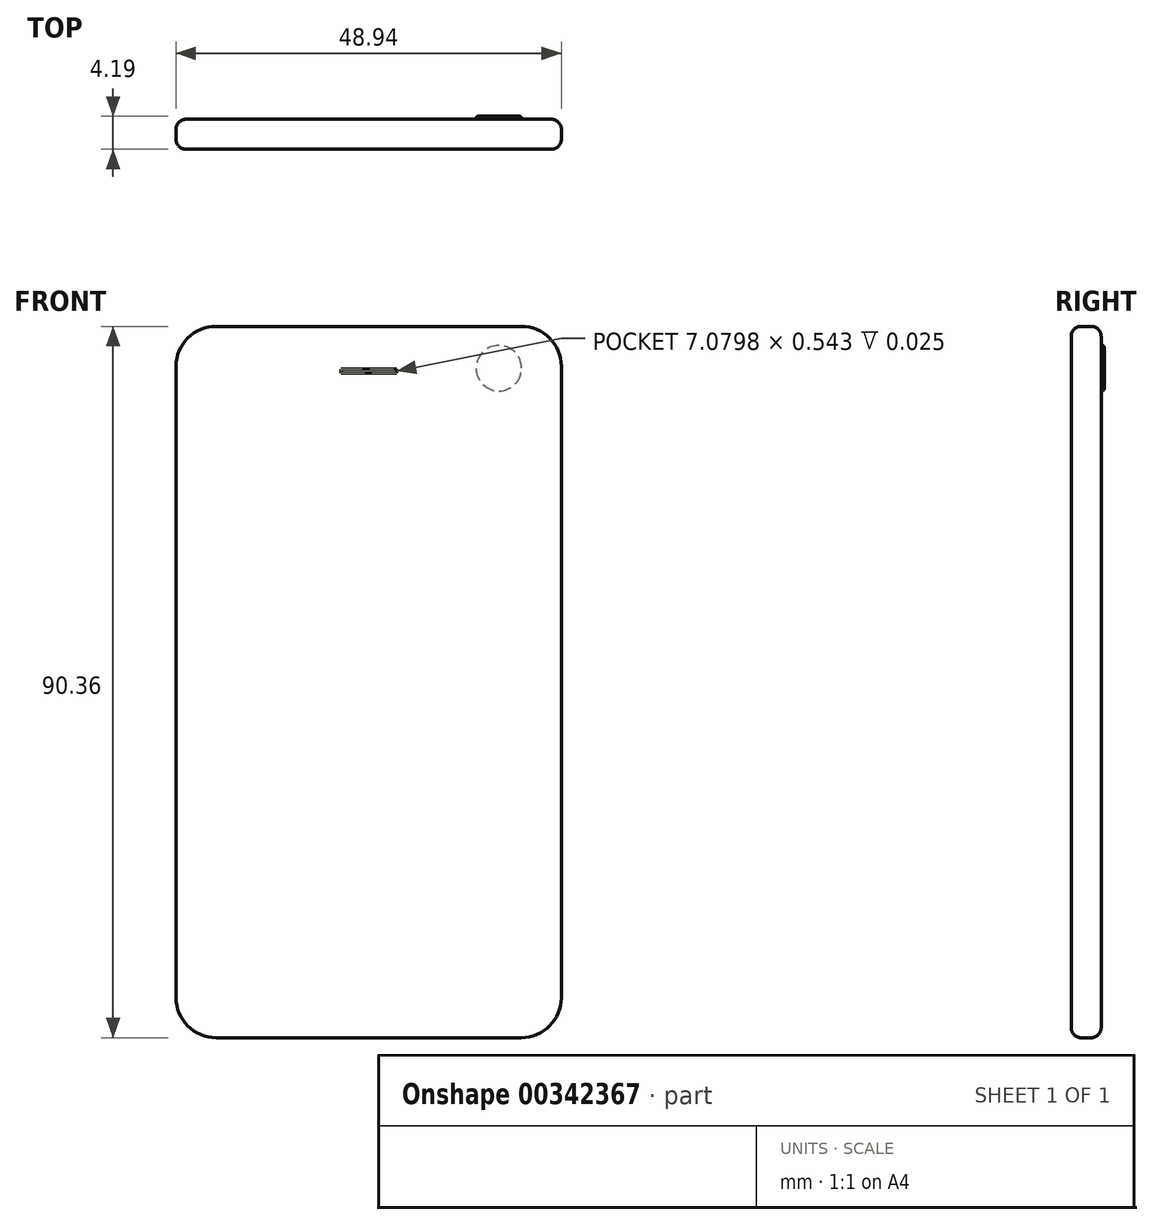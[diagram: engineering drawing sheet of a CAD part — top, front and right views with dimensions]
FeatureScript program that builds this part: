
annotation { "Feature Type Name" : "Feature", "Feature Type Description" : "" }
export const myFeature = defineFeature(function(context is Context, id is Id, definition is map)
    precondition{}
    {
        {
            var Q0;
            Q0=qCreatedBy(makeId("Front.planeOp"),FACE);
            var sketch = newSketch(context, id + "F0", { "sketchPlane" : qUnion([Q0])});
            skLineSegment(sketch, "E0.bottom", {"start": v(24.47, -45.18) * mm, "end": v(-24.47, -45.18) * mm});
            skLineSegment(sketch, "E0.top", {"start": v(24.47, 45.18) * mm, "end": v(-24.47, 45.18) * mm});
            skLineSegment(sketch, "E0.left", {"start": v(24.47, -45.18) * mm, "end": v(24.47, 45.18) * mm});
            skLineSegment(sketch, "E0.right", {"start": v(-24.47, -45.18) * mm, "end": v(-24.47, 45.18) * mm});
            skPoint(sketch, "E0.middle", {"position": v(0, 0) * mm});
            skSolve(sketch);
        }
        {
            var Q0;
            Q0=makeQuery(id+"F0.imprint","IMPRINT",FACE,{"disambiguationData":[TD([[makeQuery(id+"F0.imprint","IMPRINT",EDGE,{"derivedFrom":sQuery(id+"F0.wireOp",EDGE,"E0.bottom")}),-1.0]])]});
            extrude(context, id + "F1", {"entities" : qUnion([Q0]), "depth" : 3.8 * mm});
        }
        {
            var Q0;
            Q0=makeQuery(id+"F1.opExtrude","SWEPT_EDGE",EDGE,{"disambiguationData":[OSD([sQuery(id+"F0.wireOp",EDGE,"E0.top"),sQuery(id+"F0.wireOp",EDGE,"E0.right")])]});
            var Q1;
            Q1=makeQuery(id+"F1.opExtrude","SWEPT_EDGE",EDGE,{"disambiguationData":[OSD([sQuery(id+"F0.wireOp",EDGE,"E0.top"),sQuery(id+"F0.wireOp",EDGE,"E0.left")])]});
            var Q2;
            Q2=makeQuery(id+"F1.opExtrude","SWEPT_EDGE",EDGE,{"disambiguationData":[OSD([sQuery(id+"F0.wireOp",EDGE,"E0.bottom"),sQuery(id+"F0.wireOp",EDGE,"E0.left")])]});
            var Q3;
            Q3=makeQuery(id+"F1.opExtrude","SWEPT_EDGE",EDGE,{"disambiguationData":[OSD([sQuery(id+"F0.wireOp",EDGE,"E0.bottom"),sQuery(id+"F0.wireOp",EDGE,"E0.right")])]});
            fillet(context, id + "F2", {"entities" : qUnion([Q0, Q1, Q2, Q3]), "radius" : 5.08 * mm, "tangentPropagation" : true, "allowEdgeOverflow" : false});
        }
        {
            var Q0;
            Q0=makeQuery(id+"F1.opExtrude","CAP_EDGE",EDGE,{"disambiguationData":[OSD([sQuery(id+"F0.wireOp",EDGE,"E0.left")])],"isStart":true});
            fillet(context, id + "F3", {"entities" : qUnion([Q0]), "radius" : 1.27 * mm, "tangentPropagation" : true, "allowEdgeOverflow" : false});
        }
        {
            var Q0;
            Q0=makeQuery(id+"F1.opExtrude","CAP_EDGE",EDGE,{"disambiguationData":[OSD([sQuery(id+"F0.wireOp",EDGE,"E0.top")])],"isStart":false});
            fillet(context, id + "F4", {"entities" : qUnion([Q0]), "radius" : 1.27 * mm, "tangentPropagation" : true, "allowEdgeOverflow" : false});
        }
        {
            var Q0;
            Q0=makeQuery(id+"F1.opExtrude","CAP_FACE",FACE,{"disambiguationData":[OSD([sQuery(id+"F0.wireOp",EDGE,"E0.bottom"),sQuery(id+"F0.wireOp",EDGE,"E0.top"),sQuery(id+"F0.wireOp",EDGE,"E0.left"),sQuery(id+"F0.wireOp",EDGE,"E0.right")])],"isStart":false});
            var sketch = newSketch(context, id + "F5", { "sketchPlane" : qUnion([Q0])});
            skLineSegment(sketch, "E1.bottom", {"start": v(21.18, -35.06) * mm, "end": v(-21.18, -35.06) * mm});
            skLineSegment(sketch, "E1.top", {"start": v(21.18, 35.06) * mm, "end": v(-21.18, 35.06) * mm});
            skLineSegment(sketch, "E1.left", {"start": v(21.18, -35.06) * mm, "end": v(21.18, 35.06) * mm});
            skLineSegment(sketch, "E1.right", {"start": v(-21.18, -35.06) * mm, "end": v(-21.18, 35.06) * mm});
            skPoint(sketch, "E1.middle", {"position": v(0, 0) * mm});
            skSolve(sketch);
        }
        {
            var Q0;
            Q0=makeQuery(id+"F5.imprint","IMPRINT",FACE,{"disambiguationData":[TD([[makeQuery(id+"F5.imprint","IMPRINT",EDGE,{"derivedFrom":sQuery(id+"F5.wireOp",EDGE,"E1.bottom")}),1.0]])]});
            var sketch = newSketch(context, id + "F6", { "sketchPlane" : qUnion([Q0])});
            skCircle(sketch, "E2", {"center": v(0, -39.3) * mm, "radius": 3.86 * mm});
            skCircle(sketch, "E3", {"center": v(0, -39.3) * mm, "radius": 3.2 * mm});
            skSolve(sketch);
        }
        {
            var Q0;
            Q0=makeQuery(id+"F5.imprint","IMPRINT",FACE,{"disambiguationData":[TD([[makeQuery(id+"F5.imprint","IMPRINT",EDGE,{"derivedFrom":sQuery(id+"F5.wireOp",EDGE,"E1.bottom")}),1.0]])]});
            var sketch = newSketch(context, id + "F7", { "sketchPlane" : qUnion([Q0])});
            skLineSegment(sketch, "E4.bottom", {"start": v(3.54, 39.24) * mm, "end": v(-3.54, 39.24) * mm});
            skLineSegment(sketch, "E4.top", {"start": v(3.54, 39.78) * mm, "end": v(-3.54, 39.78) * mm});
            skLineSegment(sketch, "E4.left", {"start": v(3.54, 39.24) * mm, "end": v(3.54, 39.78) * mm});
            skLineSegment(sketch, "E4.right", {"start": v(-3.54, 39.24) * mm, "end": v(-3.54, 39.78) * mm});
            skPoint(sketch, "E4.middle", {"position": v(0, 39.5) * mm});
            skSolve(sketch);
        }
        {
            var Q0;
            Q0=makeQuery(id+"F7.imprint","IMPRINT",FACE,{"disambiguationData":[TD([[makeQuery(id+"F7.imprint","IMPRINT",EDGE,{"derivedFrom":sQuery(id+"F7.wireOp",EDGE,"E4.bottom")}),-1.0]])]});
            extrude(context, id + "F8", {"entities" : qUnion([Q0]), "operationType" : NewBodyOperationType.REMOVE, "oppositeDirection" : true, "depth" : 0.03 * mm});
        }
        {
            var Q0;
            Q0=sQuery(id+"F6.wireOp",EDGE,"E3");
            extrude(context, id + "F9", {"bodyType" : ToolBodyType.SURFACE, "operationType" : NewBodyOperationType.REMOVE, "surfaceEntities" : qUnion([Q0]), "oppositeDirection" : true, "depth" : 0.25 * mm});
        }
        {
            var Q0;
            Q0=makeQuery(id+"F1.opExtrude","CAP_FACE",FACE,{"disambiguationData":[OSD([sQuery(id+"F0.wireOp",EDGE,"E0.bottom"),sQuery(id+"F0.wireOp",EDGE,"E0.top"),sQuery(id+"F0.wireOp",EDGE,"E0.left"),sQuery(id+"F0.wireOp",EDGE,"E0.right")])],"isStart":true});
            var sketch = newSketch(context, id + "F10", { "sketchPlane" : qUnion([Q0])});
            skCircle(sketch, "E5", {"center": v(-16.54, 39.86) * mm, "radius": 2.9 * mm});
            skCircle(sketch, "E6", {"center": v(-9.53, 39.58) * mm, "radius": 1.68 * mm});
            skPoint(sketch, "E7.center.orphan", {"position": v(-12.15, 39.58) * mm});
            skCircle(sketch, "E8", {"center": v(-12.47, 39.58) * mm, "radius": 0.25 * mm});
            skLineSegment(sketch, "E9", {"start": v(-11.21, 39.58) * mm, "end": v(-7.85, 39.58) * mm});
            skSolve(sketch);
        }
        {
            var Q0;
            Q0=makeQuery(id+"F10.imprint","IMPRINT",FACE,{"disambiguationData":[TD([[makeQuery(id+"F10.imprint","IMPRINT",EDGE,{"derivedFrom":sQuery(id+"F10.wireOp",EDGE,"E5")}),1.0]])]});
            extrude(context, id + "F11", {"entities" : qUnion([Q0]), "operationType" : NewBodyOperationType.ADD, "depth" : 0.38 * mm});
        }
        {
            var Q0;
            Q0=makeQuery(id+"F11.opExtrude","CAP_EDGE",EDGE,{"disambiguationData":[OSD([sQuery(id+"F10.wireOp",EDGE,"E5")])],"isStart":false});
            fillet(context, id + "F12", {"entities" : qUnion([Q0]), "radius" : 0.25 * mm, "tangentPropagation" : true, "allowEdgeOverflow" : false});
        }
    });
